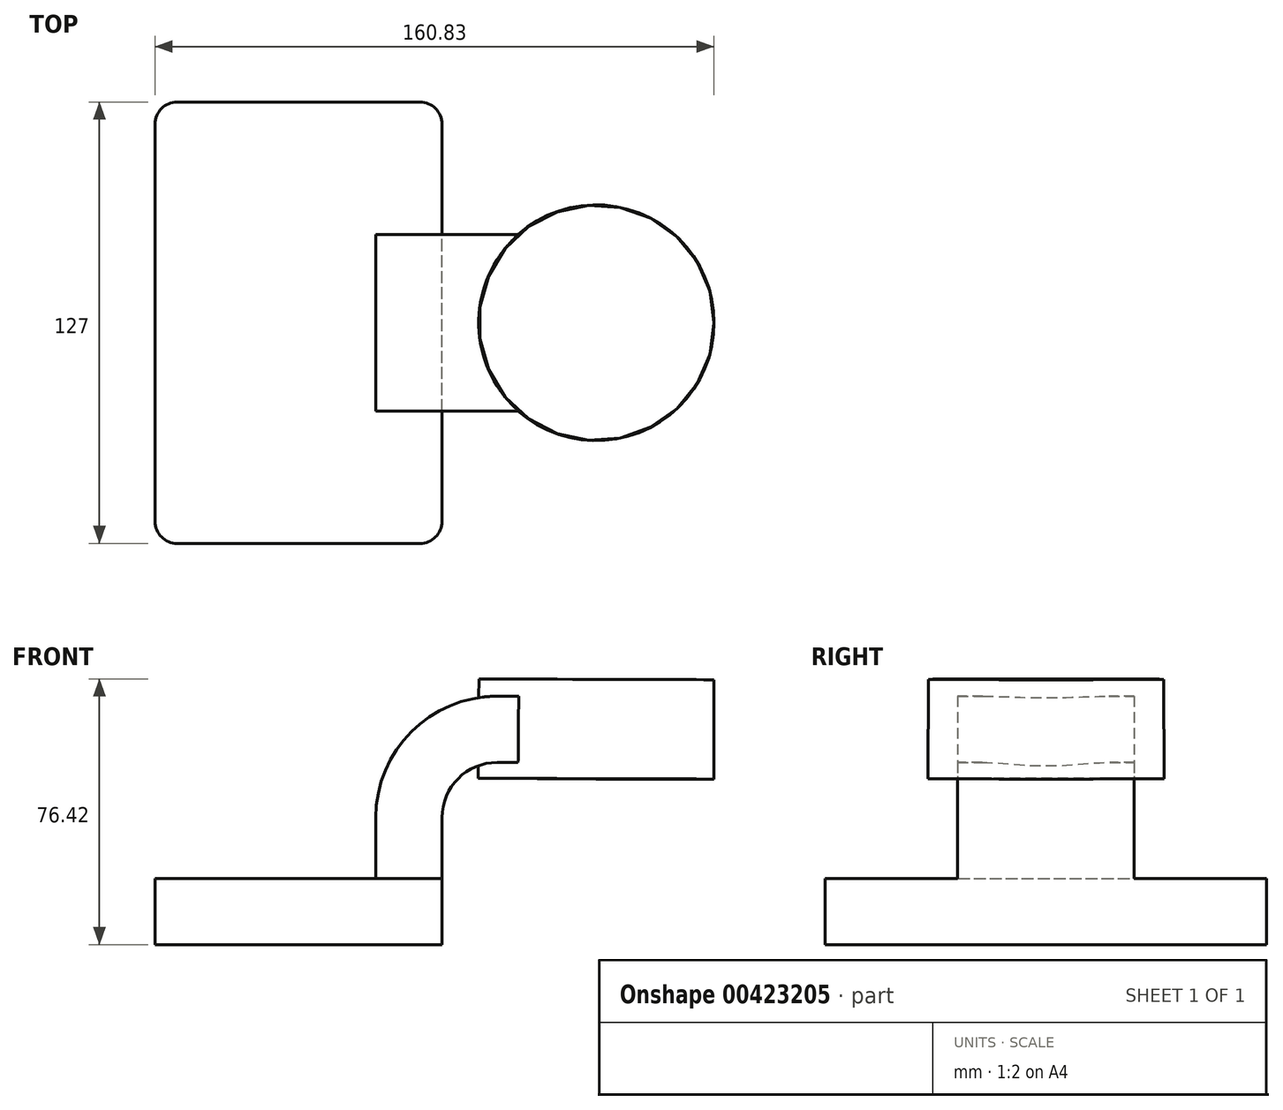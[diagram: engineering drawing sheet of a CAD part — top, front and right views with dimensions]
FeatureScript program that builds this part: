
annotation { "Feature Type Name" : "Feature", "Feature Type Description" : "" }
export const myFeature = defineFeature(function(context is Context, id is Id, definition is map)
    precondition{}
    {
        {
            var Q0;
            Q0=qCreatedBy(makeId("Front.planeOp"),FACE);
            var sketch = newSketch(context, id + "F0", { "sketchPlane" : qUnion([Q0])});
            skLineSegment(sketch, "E0.bottom", {"start": v(-41.28, 9.52) * mm, "end": v(41.27, 9.53) * mm});
            skLineSegment(sketch, "E0.top", {"start": v(-41.28, -9.53) * mm, "end": v(41.28, -9.53) * mm});
            skLineSegment(sketch, "E0.left", {"start": v(-41.28, 9.52) * mm, "end": v(-41.27, -9.53) * mm});
            skLineSegment(sketch, "E0.right", {"start": v(41.28, 9.53) * mm, "end": v(41.28, -9.52) * mm});
            skPoint(sketch, "E0.middle", {"position": v(0, 0) * mm});
            skLineSegment(sketch, "E1.bottom", {"start": v(68.76, 66.67) * mm, "end": v(119.56, 66.67) * mm});
            skLineSegment(sketch, "E1.top", {"start": v(68.76, 38.1) * mm, "end": v(119.56, 38.1) * mm});
            skLineSegment(sketch, "E1.right", {"start": v(119.56, 66.67) * mm, "end": v(119.56, 38.1) * mm});
            skPoint(sketch, "E1.middle", {"position": v(94.16, 52.39) * mm});
            skLineSegment(sketch, "E2", {"start": v(41.27, 9.53) * mm, "end": v(41.27, 27) * mm});
            skArc(sketch, "E3", {"start": v(41.27, 27) * mm, "mid": v(45.92, 38.23) * mm, "end": v(57.15, 42.88) * mm});
            skLineSegment(sketch, "E4", {"start": v(57.15, 42.88) * mm, "end": v(85.73, 42.88) * mm});
            skLineSegment(sketch, "E5.0", {"start": v(57.15, 61.93) * mm, "end": v(85.73, 61.93) * mm});
            skArc(sketch, "E5.1", {"start": v(22.22, 27) * mm, "mid": v(32.45, 51.7) * mm, "end": v(57.15, 61.93) * mm});
            skLineSegment(sketch, "E5.2", {"start": v(22.22, 9.53) * mm, "end": v(22.22, 27) * mm});
            skFitSpline(sketch, "E6", {"points": [v(-41.28, 9.52) * mm, v(68.76, 61.93) * mm], "startDerivative": vector(5.08, 126.5) * mm, "endDerivative": vector(91.9, -15.3) * mm});
            skLineSegment(sketch, "E7", {"start": v(85.63, 38.1) * mm, "end": v(85.73, 66.67) * mm});
            skLineSegment(sketch, "E8", {"start": v(68.76, 66.67) * mm, "end": v(68.76, 61.93) * mm});
            skLineSegment(sketch, "E9", {"start": v(68.76, 38.1) * mm, "end": v(68.76, 42.88) * mm});
            skSolve(sketch);
        }
        {
            var Q0;
            Q0=makeQuery(id+"F0.imprint","IMPRINT",FACE,{"disambiguationData":[TD([[makeQuery(id+"F0.imprint","IMPRINT",EDGE,{"derivedFrom":sQuery(id+"F0.wireOp",EDGE,"E0.top")}),1.0]])]});
            extrude(context, id + "F1", {"entities" : qUnion([Q0]), "endBound" : BoundingType.SYMMETRIC, "depth" : 127 * mm});
        }
        {
            var Q0;
            {var subQ3=sQuery(id+"F0.wireOp",EDGE,"E2");Q0=makeQuery(id+"F0.imprint","IMPRINT",FACE,{"disambiguationData":[TD([[makeQuery(id+"F0.imprint","IMPRINT",EDGE,{"derivedFrom":subQ3}),1.0]])]});}
            extrude(context, id + "F2", {"entities" : qUnion([Q0]), "operationType" : NewBodyOperationType.ADD, "endBound" : BoundingType.SYMMETRIC, "depth" : 50.8 * mm});
        }
        {
            var Q0;
            {var subQ1=sQuery(id+"F0.wireOp",EDGE,"E5.1");Q0=makeQuery(id+"F0.imprint","IMPRINT",FACE,{"disambiguationData":[TD([[makeQuery(id+"F0.imprint","IMPRINT",EDGE,{"derivedFrom":subQ1}),1.0]])]});}
            extrude(context, id + "F3", {"entities" : qUnion([Q0]), "operationType" : NewBodyOperationType.ADD, "depth" : 15.88 * mm});
        }
        {
            var Q0;
            {var subQ4=sQuery(id+"F0.wireOp",EDGE,"E1.right");Q0=makeQuery(id+"F0.imprint","IMPRINT",FACE,{"disambiguationData":[TD([[makeQuery(id+"F0.imprint","IMPRINT",EDGE,{"derivedFrom":subQ4}),-1.0]])]});}
            var Q1;
            Q1=sQuery(id+"F0.wireOp",EDGE,"E7");
            revolve(context, id + "F4", {"operationType" : NewBodyOperationType.ADD, "entities" : qUnion([Q0]), "axis" : qUnion([Q1]), "revolveType" : RevolveType.SYMMETRIC, "oppositeDirection" : true, "angle" : 360 * degree});
        }
        {
            var Q0;
            Q0=makeQuery(id+"F1.opExtrude","CAP_EDGE",EDGE,{"disambiguationData":[OSD([sQuery(id+"F0.wireOp",EDGE,"E0.left")])],"isStart":false});
            var Q1;
            Q1=makeQuery(id+"F1.opExtrude","CAP_EDGE",EDGE,{"disambiguationData":[OSD([sQuery(id+"F0.wireOp",EDGE,"E0.right")])],"isStart":false});
            var Q2;
            Q2=makeQuery(id+"F1.opExtrude","CAP_EDGE",EDGE,{"disambiguationData":[OSD([sQuery(id+"F0.wireOp",EDGE,"E0.right")])],"isStart":true});
            var Q3;
            Q3=makeQuery(id+"F1.opExtrude","CAP_EDGE",EDGE,{"disambiguationData":[OSD([sQuery(id+"F0.wireOp",EDGE,"E0.left")])],"isStart":true});
            fillet(context, id + "F5", {"entities" : qUnion([Q0, Q1, Q2, Q3]), "radius" : 6.35 * mm, "tangentPropagation" : true, "allowEdgeOverflow" : false});
        }
    });
